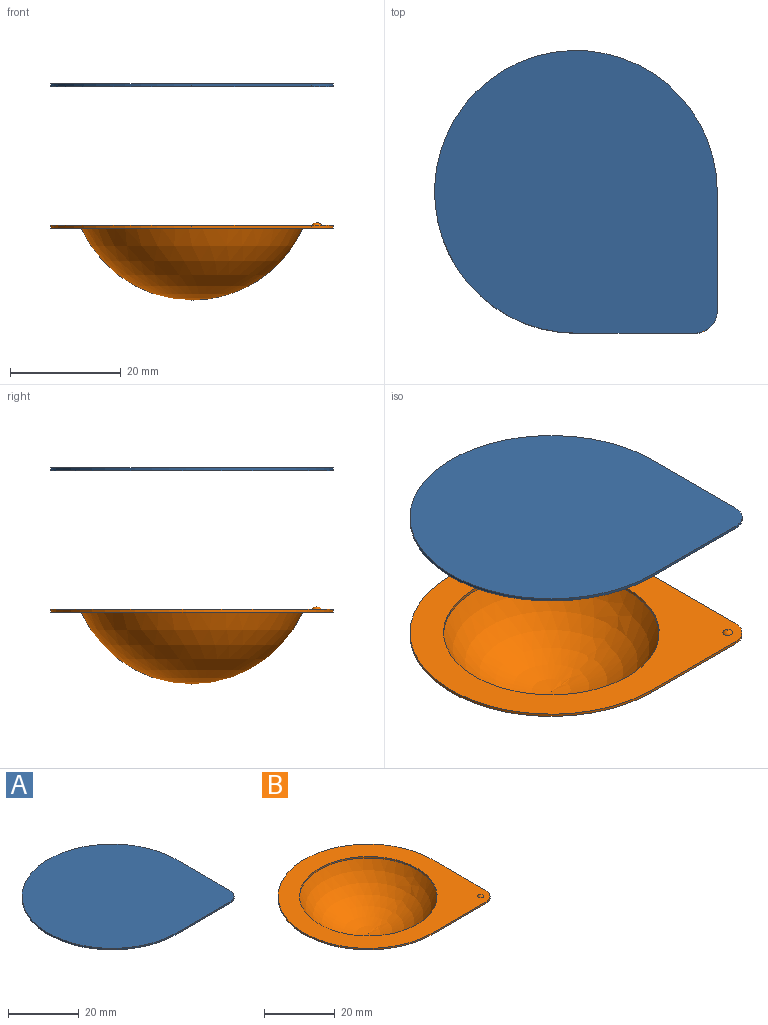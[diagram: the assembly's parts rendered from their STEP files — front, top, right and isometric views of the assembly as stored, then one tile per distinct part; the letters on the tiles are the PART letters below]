
ASSEMBLY  parts=2 mates=1
PART A: 6 faces, bbox 51x51x0.5 mm
  f0: plane 21.5x0.5mm, normal (1,0,0), area 10.8mm2, adj f1,f3,f4,f5
  f1: cylinder r=25.5mm len=51mm, axis (0,0,-1), area 60.1mm2, adj f0,f2,f4,f5
  f2: plane 21.5x0.5mm, normal (0,-1,0), area 10.8mm2, adj f1,f3,f4,f5
  f3: cylinder r=4mm len=4mm, axis (0,0,-1), area 3.1mm2, adj f0,f2,f4,f5
  f4: plane 51x51mm, normal (0,0,1), area 2178.9mm2, adj f0,f1,f2,f3
  f5: plane 51x51mm, normal (0,0,-1), area 2178.9mm2, adj f0,f1,f2,f3
PART B: 10 faces, bbox 51x51x14 mm
  f0: sphere r=21.88mm, area 1787.6mm2, adj f1
  f1: plane 51x51mm, normal (0,0,-1), area 922.3mm2, adj f0,f2,f3,f4,f5
  f2: plane 21.5x0.5mm, normal (1,0,0), area 10.8mm2, adj f1,f3,f5,f7
  f3: cylinder r=25.5mm len=51mm, axis (0,0,-1), area 60.1mm2, adj f1,f2,f4,f7
  f4: plane 21.5x0.5mm, normal (0,-1,0), area 10.8mm2, adj f1,f3,f5,f7
  f5: cylinder r=4mm len=4mm, axis (0,0,-1), area 3.1mm2, adj f1,f2,f4,f7
  f6: cylinder r=19.45mm len=38.9mm, axis (0,0,-1), area 61.1mm2, adj f7,f8
  f7: plane 51x51mm, normal (0,0,1), area 987.9mm2, adj f2,f3,f4,f5,f6,f9
  f8: sphere r=21.38mm, area 1679.5mm2, adj f6
  f9: sphere r=1mm, area 3.1mm2, adj f7
PLACE A t=(-14.55,-13.82,23.36)mm
PLACE B t=(-14.55,-13.82,-2.14)mm
MATE fastened A.f1 <-> B.f6  axis (0,0,-1) through (-14.55,-13.82,23.36)mm
